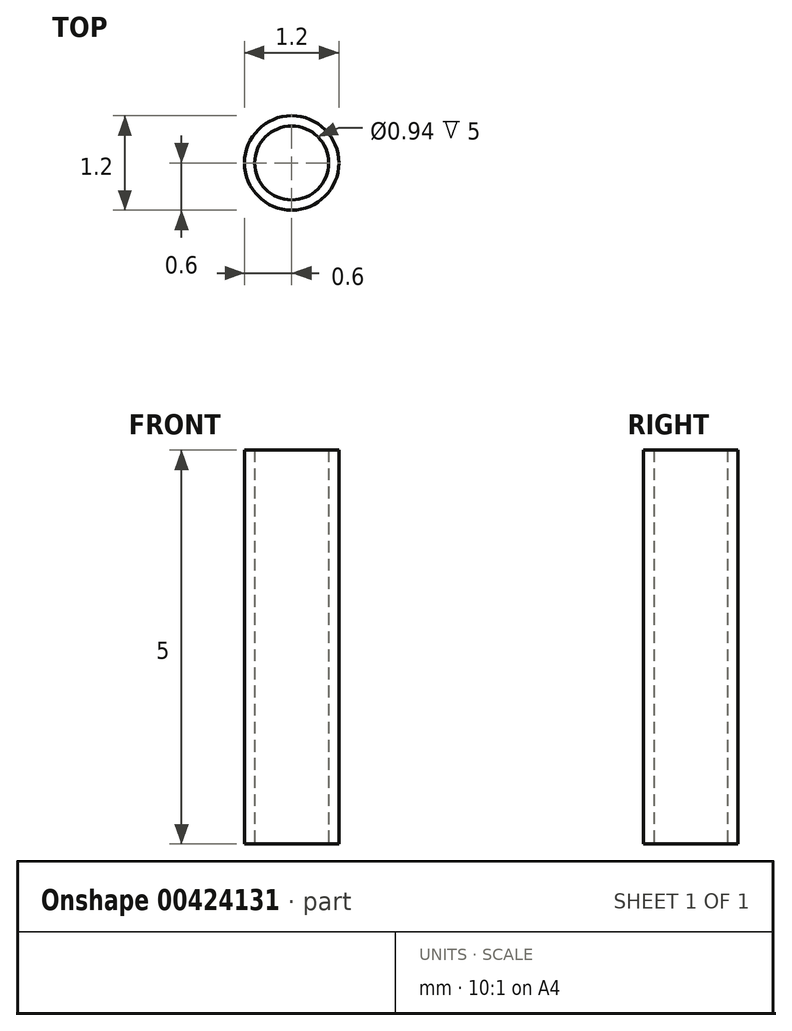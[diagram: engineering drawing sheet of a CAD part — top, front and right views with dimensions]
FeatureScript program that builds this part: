
annotation { "Feature Type Name" : "Feature", "Feature Type Description" : "" }
export const myFeature = defineFeature(function(context is Context, id is Id, definition is map)
    precondition{}
    {
        {
            var Q0;
            Q0=qCreatedBy(makeId("Top.planeOp"),FACE);
            var sketch = newSketch(context, id + "F0", { "sketchPlane" : qUnion([Q0])});
            skCircle(sketch, "E0", {"center": v(0, 0) * mm, "radius": 0.6 * mm});
            skCircle(sketch, "E1", {"center": v(0, 0) * mm, "radius": 0.47 * mm});
            skSolve(sketch);
        }
        {
            var Q0;
            Q0 = qSketchRegion(id + "F0", true);
            extrude(context, id + "F1", {"entities" : qUnion([Q0]), "depth" : 5 * mm});
        }
    });
